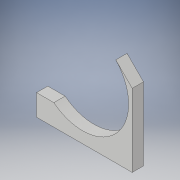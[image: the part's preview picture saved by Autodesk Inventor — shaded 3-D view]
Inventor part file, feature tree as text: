
AUTODESK INVENTOR PART (.ipt)
format: ipt  version: 2018 (Build 220112000, 112)  size: 107,008 bytes
history: native  units: in
note: dims shown in document units (in); Inventor stores cm internally (conversion verified against a paired STEP export)
features: extrude x1, sketch x1
ambient origin geometry x8: Origin, YZ Plane, XZ Plane, XY Plane, X Axis, Y Axis, Z Axis, Center Point
bodies: Solid1 (feature_tree)
feature tree (2):
  extrude  "Extrusion1"  TaperAngle=135.0deg  [1 undecoded]
  sketch  "Sketch1"  dims[d0=16.375in d3=135.0deg d4=2.0in d5=0.0in d6=17.0in d7=2.0in]
note: 1 required parameter value undecoded (feature->parameter linkage not recoverable at this tier; creation-order binding heuristic only, values carry confidence <= 0.55)
